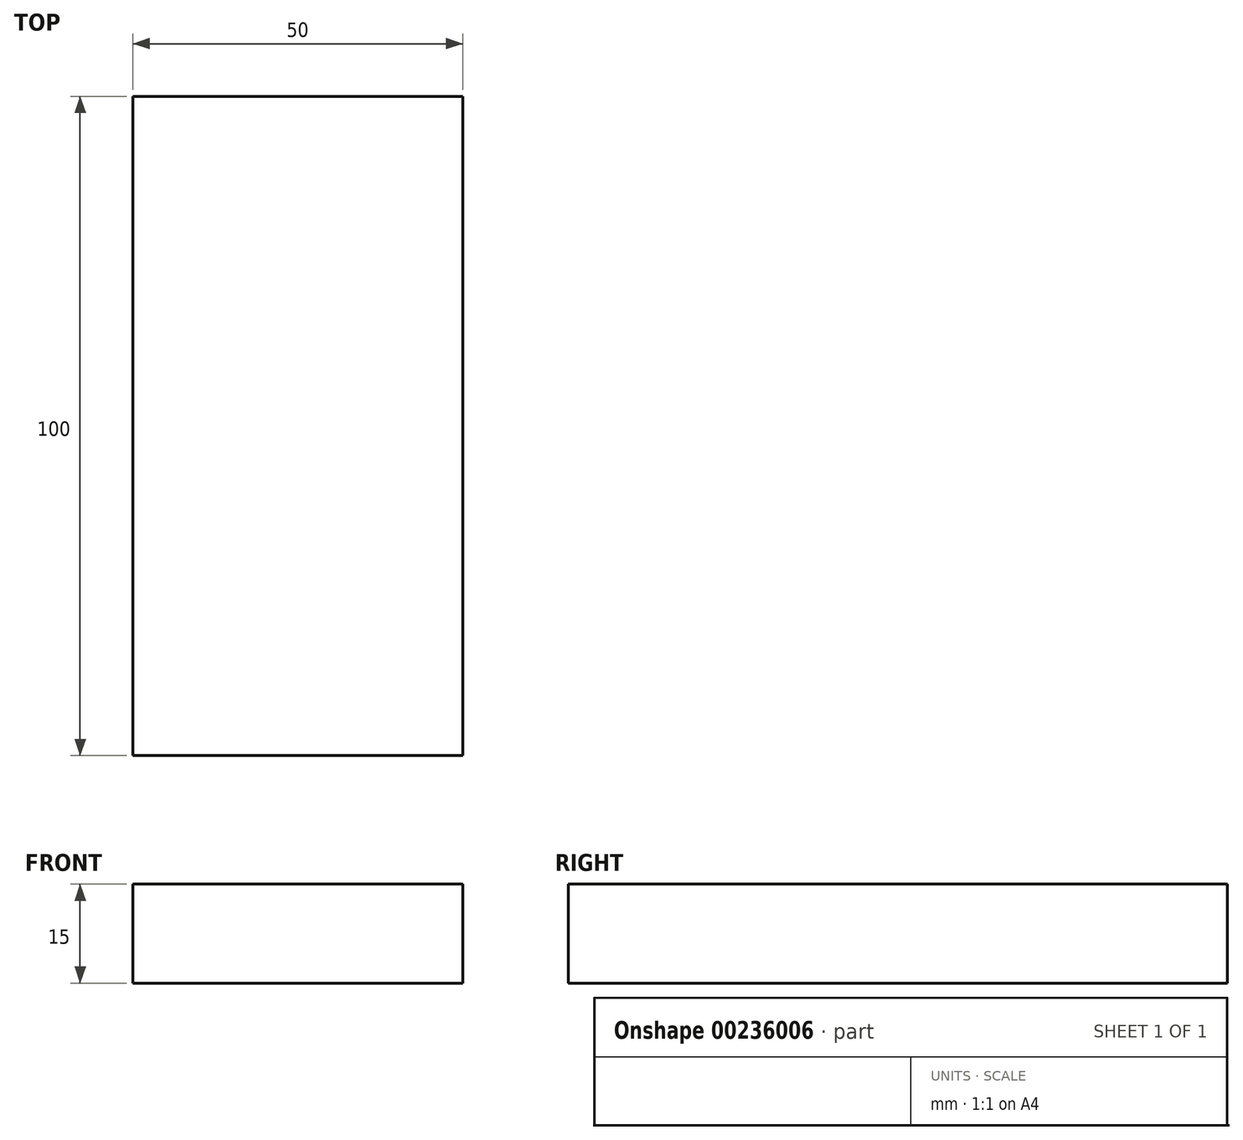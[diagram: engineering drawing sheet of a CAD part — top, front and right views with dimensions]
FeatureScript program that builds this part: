
annotation { "Feature Type Name" : "Feature", "Feature Type Description" : "" }
export const myFeature = defineFeature(function(context is Context, id is Id, definition is map)
    precondition{}
    {
        {
            var Q0;
            Q0=qCreatedBy(makeId("Top.planeOp"),FACE);
            var sketch = newSketch(context, id + "F0", { "sketchPlane" : qUnion([Q0])});
            skLineSegment(sketch, "E0.bottom", {"start": v(-25, 50) * mm, "end": v(25, 50) * mm});
            skLineSegment(sketch, "E0.top", {"start": v(-25, -50) * mm, "end": v(25, -50) * mm});
            skLineSegment(sketch, "E0.left", {"start": v(-25, 50) * mm, "end": v(-25, -50) * mm});
            skLineSegment(sketch, "E0.right", {"start": v(25, 50) * mm, "end": v(25, -50) * mm});
            skPoint(sketch, "E0.middle", {"position": v(0, 0) * mm});
            skSolve(sketch);
        }
        {
            var Q0;
            Q0=makeQuery(id+"F0.imprint","IMPRINT",FACE,{"disambiguationData":[TD([[makeQuery(id+"F0.imprint","IMPRINT",EDGE,{"derivedFrom":sQuery(id+"F0.wireOp",EDGE,"E0.bottom")}),-1.0]])]});
            extrude(context, id + "F1", {"entities" : qUnion([Q0]), "depth" : 15 * mm});
        }
    });
